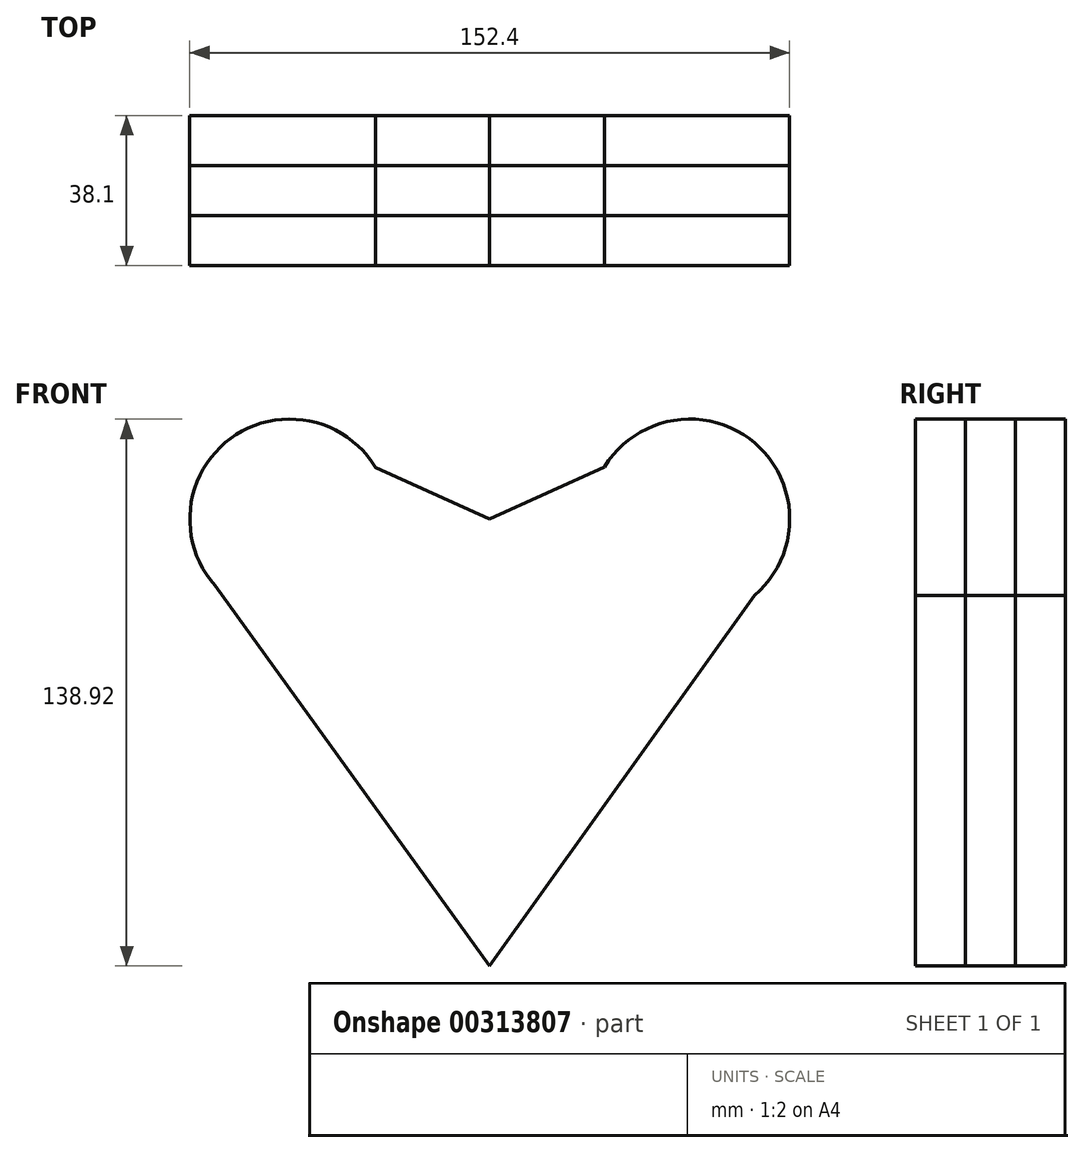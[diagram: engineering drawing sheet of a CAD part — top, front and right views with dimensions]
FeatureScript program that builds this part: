
annotation { "Feature Type Name" : "Feature", "Feature Type Description" : "" }
export const myFeature = defineFeature(function(context is Context, id is Id, definition is map)
    precondition{}
    {
        {
            var Q0;
            Q0=qCreatedBy(makeId("Front.planeOp"),FACE);
            var sketch = newSketch(context, id + "F0", { "sketchPlane" : qUnion([Q0])});
            skLineSegment(sketch, "E0.bottom", {"start": v(-25.4, 25.4) * mm, "end": v(25.4, 25.4) * mm});
            skLineSegment(sketch, "E0.top", {"start": v(-25.4, -25.4) * mm, "end": v(25.4, -25.4) * mm});
            skLineSegment(sketch, "E0.left", {"start": v(-25.4, 25.4) * mm, "end": v(-25.4, -25.4) * mm});
            skLineSegment(sketch, "E0.right", {"start": v(25.4, 25.4) * mm, "end": v(25.4, -25.4) * mm});
            skPoint(sketch, "E0.middle", {"position": v(0, 0) * mm});
            skLineSegment(sketch, "E1", {"start": v(-25.4, 25.4) * mm, "end": v(25.4, -25.4) * mm, "construction": true});
            skLineSegment(sketch, "E2", {"start": v(-25.4, -25.4) * mm, "end": v(25.4, 25.4) * mm, "construction": true});
            skLineSegment(sketch, "E3", {"start": v(-119.49, 79.24) * mm, "end": v(-124.4, 84.15) * mm, "construction": true});
            skCircle(sketch, "E4", {"center": v(50.8, 25.4) * mm, "radius": 25.4 * mm});
            skCircle(sketch, "E5", {"center": v(-50.8, 25.4) * mm, "radius": 25.4 * mm});
            skLineSegment(sketch, "E6", {"start": v(-69.8, 8.54) * mm, "end": v(0, -88.12) * mm});
            skLineSegment(sketch, "E7", {"start": v(0, -88.12) * mm, "end": v(67.24, 6.04) * mm});
            skLineSegment(sketch, "E8", {"start": v(-29.04, 38.5) * mm, "end": v(0, 25.4) * mm});
            skLineSegment(sketch, "E9", {"start": v(0, 25.4) * mm, "end": v(29.15, 38.68) * mm});
            skSolve(sketch);
        }
        {
            var Q0;
            Q0 = qSketchRegion(id + "F0", true);
            extrude(context, id + "F1", {"entities" : qUnion([Q0]), "endBound" : BoundingType.SYMMETRIC, "depth" : 25.4 * mm});
        }
        {
            var Q0;
            Q0 = qSketchRegion(id + "F0", true);
            extrude(context, id + "F2", {"entities" : qUnion([Q0]), "depth" : 25.4 * mm});
        }
    });
